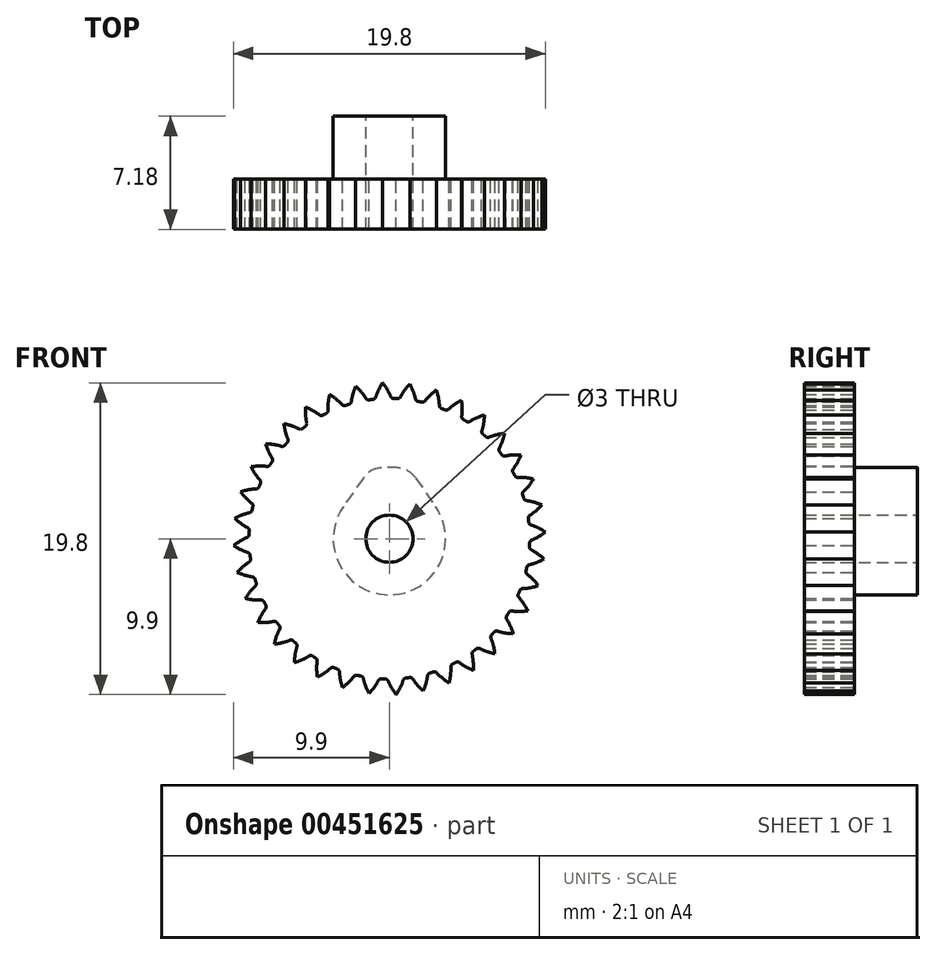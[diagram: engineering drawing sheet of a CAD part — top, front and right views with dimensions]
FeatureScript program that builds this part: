
annotation { "Feature Type Name" : "Feature", "Feature Type Description" : "" }
export const myFeature = defineFeature(function(context is Context, id is Id, definition is map)
    precondition{}
    {
        {
            assignVariable(context, id + "F0", {"name" : "Teeth", "anyValue" : 36});
        }
        {
            var Q0;
            Q0=qCreatedBy(makeId("Front.planeOp"),FACE);
            var sketch = newSketch(context, id + "F1", { "sketchPlane" : qUnion([Q0])});
            skCircle(sketch, "E0", {"center": v(0, 0) * mm, "radius": 8.49 * mm, "construction": true});
            skLineSegment(sketch, "E1", {"start": v(0, 0) * mm, "end": v(-0.32, 8.48) * mm, "construction": true});
            skLineSegment(sketch, "E2", {"start": v(0, 0) * mm, "end": v(-0.87, 8.44) * mm, "construction": true});
            skLineSegment(sketch, "E3", {"start": v(0, 0) * mm, "end": v(-1.41, 8.37) * mm, "construction": true});
            skLineSegment(sketch, "E4", {"start": v(-1.41, 8.37) * mm, "end": v(0.2, 8.64) * mm, "construction": true});
            skLineSegment(sketch, "E5", {"start": v(0, 0) * mm, "end": v(-1.95, 8.26) * mm, "construction": true});
            skLineSegment(sketch, "E6", {"start": v(-1.95, 8.26) * mm, "end": v(0.18, 8.76) * mm, "construction": true});
            skLineSegment(sketch, "E7", {"start": v(-1.41, 8.37) * mm, "end": v(-0.87, 8.44) * mm, "construction": true});
            skLineSegment(sketch, "E8", {"start": v(-1.95, 8.26) * mm, "end": v(-1.41, 8.37) * mm, "construction": true});
            skLineSegment(sketch, "E9", {"start": v(-1.41, 8.37) * mm, "end": v(-0.32, 8.48) * mm, "construction": true});
            skLineSegment(sketch, "E10", {"start": v(-1.95, 8.26) * mm, "end": v(-0.32, 8.48) * mm, "construction": true});
            skLineSegment(sketch, "E11", {"start": v(0, 0) * mm, "end": v(-3.5, 7.73) * mm, "construction": true});
            skLineSegment(sketch, "E12", {"start": v(-3.5, 7.73) * mm, "end": v(-0.04, 9.3) * mm, "construction": true});
            skLineSegment(sketch, "E13", {"start": v(0, 0) * mm, "end": v(-3, 7.94) * mm, "construction": true});
            skLineSegment(sketch, "E14", {"start": v(-3, 7.94) * mm, "end": v(0.06, 9.1) * mm, "construction": true});
            skLineSegment(sketch, "E15", {"start": v(0, 0) * mm, "end": v(-2.48, 8.12) * mm, "construction": true});
            skLineSegment(sketch, "E16", {"start": v(-2.48, 8.12) * mm, "end": v(0.13, 8.91) * mm, "construction": true});
            skLineSegment(sketch, "E17", {"start": v(-2.48, 8.12) * mm, "end": v(-1.95, 8.26) * mm, "construction": true});
            skLineSegment(sketch, "E18", {"start": v(-2.48, 8.12) * mm, "end": v(-3, 7.94) * mm, "construction": true});
            skLineSegment(sketch, "E19", {"start": v(-3, 7.94) * mm, "end": v(-3.5, 7.73) * mm, "construction": true});
            skLineSegment(sketch, "E20", {"start": v(-2.48, 8.12) * mm, "end": v(-0.32, 8.48) * mm, "construction": true});
            skLineSegment(sketch, "E21", {"start": v(-3, 7.94) * mm, "end": v(-0.32, 8.48) * mm, "construction": true});
            skLineSegment(sketch, "E22", {"start": v(-3.5, 7.73) * mm, "end": v(-0.32, 8.48) * mm, "construction": true});
            skLineSegment(sketch, "E23", {"start": v(0, 0) * mm, "end": v(-4.47, 7.21) * mm, "construction": true});
            skLineSegment(sketch, "E24", {"start": v(-4.47, 7.21) * mm, "end": v(-0.34, 9.78) * mm, "construction": true});
            skLineSegment(sketch, "E25", {"start": v(0, 0) * mm, "end": v(-4.93, 6.9) * mm, "construction": true});
            skLineSegment(sketch, "E26", {"start": v(-4.93, 6.9) * mm, "end": v(-0.54, 10.04) * mm, "construction": true});
            skLineSegment(sketch, "E27", {"start": v(0, 0) * mm, "end": v(-5.37, 6.58) * mm, "construction": true});
            skLineSegment(sketch, "E28", {"start": v(0, 0) * mm, "end": v(-4, 7.49) * mm, "construction": true});
            skLineSegment(sketch, "E29", {"start": v(-4, 7.49) * mm, "end": v(-0.17, 9.53) * mm, "construction": true});
            skLineSegment(sketch, "E30", {"start": v(-3.5, 7.73) * mm, "end": v(-4, 7.49) * mm, "construction": true});
            skLineSegment(sketch, "E31", {"start": v(-4, 7.49) * mm, "end": v(-4.47, 7.21) * mm, "construction": true});
            skLineSegment(sketch, "E32", {"start": v(-4.47, 7.21) * mm, "end": v(-4.93, 6.9) * mm, "construction": true});
            skLineSegment(sketch, "E33", {"start": v(-4.93, 6.9) * mm, "end": v(-5.37, 6.58) * mm, "construction": true});
            skLineSegment(sketch, "E34", {"start": v(-0.32, 8.48) * mm, "end": v(-4, 7.49) * mm, "construction": true});
            skLineSegment(sketch, "E35", {"start": v(-0.32, 8.48) * mm, "end": v(-4.47, 7.21) * mm, "construction": true});
            skLineSegment(sketch, "E36", {"start": v(-0.32, 8.48) * mm, "end": v(-4.93, 6.9) * mm, "construction": true});
            skLineSegment(sketch, "E37", {"start": v(-0.32, 8.48) * mm, "end": v(-5.37, 6.58) * mm, "construction": true});
            skCircle(sketch, "E38", {"center": v(0, 0) * mm, "radius": 9.53 * mm, "construction": true});
            skCircle(sketch, "E39", {"center": v(0, 0) * mm, "radius": 10.05 * mm});
            skPoint(sketch, "E40", {"position": v(0, 9.53) * mm});
            skLineSegment(sketch, "E41", {"start": v(0, 0) * mm, "end": v(-0.38, 8.6) * mm, "construction": true});
            skPoint(sketch, "E42.MirrorP", {"position": v(-0.83, 9.49) * mm});
            skLineSegment(sketch, "E43", {"start": v(-0.83, 9.49) * mm, "end": v(0, 0) * mm, "construction": true});
            skLineSegment(sketch, "E44", {"start": v(0, 0) * mm, "end": v(0, 9.53) * mm, "construction": true});
            skLineSegment(sketch, "E45", {"start": v(-0.87, 8.44) * mm, "end": v(-0.32, 8.48) * mm, "construction": true});
            skLineSegment(sketch, "E46", {"start": v(0.2, 8.64) * mm, "end": v(0.18, 8.76) * mm, "construction": true});
            skLineSegment(sketch, "E47", {"start": v(0, 0) * mm, "end": v(0, 10.19) * mm, "construction": true});
            skCircle(sketch, "E48", {"center": v(0, 0) * mm, "radius": 8.91 * mm});
            skSolve(sketch);
        }
        {
            var Q0;
            Q0=qCreatedBy(makeId("Front.planeOp"),FACE);
            var sketch = newSketch(context, id + "F2", { "sketchPlane" : qUnion([Q0])});
            skCircle(sketch, "E49.0", {"center": v(0, 0) * mm, "radius": 9.53 * mm, "construction": true});
            skPoint(sketch, "E50.0", {"position": v(-0.54, 10.04) * mm});
            skPoint(sketch, "E50.1", {"position": v(-0.34, 9.78) * mm});
            skPoint(sketch, "E50.2", {"position": v(-0.17, 9.53) * mm});
            skPoint(sketch, "E50.3", {"position": v(-0.04, 9.3) * mm});
            skPoint(sketch, "E50.4", {"position": v(0.06, 9.1) * mm});
            skPoint(sketch, "E50.6", {"position": v(0.18, 8.76) * mm});
            skPoint(sketch, "E50.7", {"position": v(0.2, 8.64) * mm});
            skPoint(sketch, "E50.8", {"position": v(0.13, 8.91) * mm});
            skLineSegment(sketch, "E51.0", {"start": v(0, 0) * mm, "end": v(-0.38, 8.6) * mm, "construction": true});
            skFitSpline(sketch, "E52", {"points": [v(-0.54, 10.04) * mm, v(-0.34, 9.78) * mm, v(-0.17, 9.53) * mm, v(-0.04, 9.3) * mm, v(0.06, 9.1) * mm, v(0.13, 8.91) * mm, v(0.18, 8.76) * mm, v(0.2, 8.64) * mm], "startDerivative": vector(3.53, -4.5) * mm, "endDerivative": vector(0.8, -3.4) * mm});
            skFitSpline(sketch, "E53.MirrorCS", {"points": [v(-0.34, 10.05) * mm, v(-0.52, 9.77) * mm, v(-0.66, 9.5) * mm, v(-0.77, 9.27) * mm, v(-0.85, 9.06) * mm, v(-0.9, 8.87) * mm, v(-0.94, 8.71) * mm, v(-0.96, 8.6) * mm], "startDerivative": vector(-3.13, -4.8) * mm, "endDerivative": vector(-0.5, -3.46) * mm});
            skCircle(sketch, "E54", {"center": v(0, 0) * mm, "radius": 1.5 * mm});
            skCircle(sketch, "E55.0", {"center": v(0, 0) * mm, "radius": 8.91 * mm});
            skArc(sketch, "E56", {"start": v(-0.54, 10.04) * mm, "mid": v(0.44, -10.04) * mm, "end": v(-0.34, 10.05) * mm});
            skLineSegment(sketch, "E57", {"start": v(-0.96, 8.6) * mm, "end": v(0, 0) * mm});
            skLineSegment(sketch, "E58", {"start": v(0, 0) * mm, "end": v(0.2, 8.64) * mm});
            skSolve(sketch);
        }
        {
            var Q0;
            {var subQ1=sQuery(id+"F2.wireOp",EDGE,"E52");var subQ9=sQuery(id+"F2.wireOp",EDGE,"rA0usyOi-Jm6w-jZNR-JSDv-ujEcH4bsm2Ol");var subQ11=makeQuery(id+"F2.imprint","INTERSECT",VERTEX,{"derivedFrom":[subQ1,subQ9]});Q0=makeQuery(id+"F2.imprint","IMPRINT",FACE,{"disambiguationData":[TD([[makeQuery(id+"F2.imprint","IMPRINT",EDGE,{"disambiguationData":[TD([[subQ11,1.0]])],"derivedFrom":subQ1}),-1.0]])]});}
            var Q1;
            {var subQ0=sQuery(id+"F2.wireOp",EDGE,"QqPcIgQ4-TZE6-73E5-WQaq-ugCT5JtziKyn");var subQ1=sQuery(id+"F2.wireOp",EDGE,"90be38e0-c88f-493d-85a8-1201295b9109.0");var subQ2=makeQuery(id+"F2.imprint","INTERSECT",VERTEX,{"derivedFrom":[subQ1,subQ0]});Q1=makeQuery(id+"F2.imprint","IMPRINT",FACE,{"disambiguationData":[TD([[makeQuery(id+"F2.imprint","IMPRINT",EDGE,{"disambiguationData":[TD([[subQ2,1.0]])],"derivedFrom":subQ1}),1.0]])]});}
            var Q2;
            {var subQ0=sQuery(id+"F2.wireOp",EDGE,"QqPcIgQ4-TZE6-73E5-WQaq-ugCT5JtziKyn");var subQ1=sQuery(id+"F2.wireOp",EDGE,"90be38e0-c88f-493d-85a8-1201295b9109.0");var subQ2=makeQuery(id+"F2.imprint","INTERSECT",VERTEX,{"derivedFrom":[subQ1,subQ0]});Q2=makeQuery(id+"F2.imprint","IMPRINT",FACE,{"disambiguationData":[TD([[makeQuery(id+"F2.imprint","IMPRINT",EDGE,{"disambiguationData":[TD([[subQ2,-1.0]])],"derivedFrom":subQ1}),1.0]])]});}
            var Q3;
            {var subQ1=sQuery(id+"F2.wireOp",EDGE,"E52");var subQ8=sQuery(id+"F2.wireOp",EDGE,"b861a5ab-cd51-40f1-92ab-cea0f5fe0d4d.1");var subQ11=makeQuery(id+"F2.imprint","INTERSECT",VERTEX,{"derivedFrom":[subQ1,subQ8]});Q3=makeQuery(id+"F2.imprint","IMPRINT",FACE,{"disambiguationData":[TD([[makeQuery(id+"F2.imprint","IMPRINT",EDGE,{"disambiguationData":[TD([[subQ11,1.0]])],"derivedFrom":subQ1}),-1.0]])]});}
            var Q4;
            {var subQ0=sQuery(id+"F2.wireOp",EDGE,"b861a5ab-cd51-40f1-92ab-cea0f5fe0d4d.0");var subQ1=sQuery(id+"F2.wireOp",EDGE,"E54");var subQ2=makeQuery(id+"F2.imprint","INTERSECT",VERTEX,{"derivedFrom":[subQ1,subQ0]});Q4=makeQuery(id+"F2.imprint","IMPRINT",FACE,{"disambiguationData":[TD([[makeQuery(id+"F2.imprint","IMPRINT",EDGE,{"disambiguationData":[TD([[subQ2,-1.0]])],"derivedFrom":subQ1}),-1.0]])]});}
            var Q5;
            {var subQ0=sQuery(id+"F2.wireOp",EDGE,"b861a5ab-cd51-40f1-92ab-cea0f5fe0d4d.0");var subQ1=sQuery(id+"F2.wireOp",EDGE,"E54");var subQ2=makeQuery(id+"F2.imprint","INTERSECT",VERTEX,{"derivedFrom":[subQ1,subQ0]});Q5=makeQuery(id+"F2.imprint","IMPRINT",FACE,{"disambiguationData":[TD([[makeQuery(id+"F2.imprint","IMPRINT",EDGE,{"disambiguationData":[TD([[subQ2,1.0]])],"derivedFrom":subQ1}),-1.0]])]});}
            extrude(context, id + "F3", {"entities" : qUnion([Q0, Q1, Q2, Q3, Q4, Q5]), "depth" : 3.17 * mm});
        }
        {
            var Q0;
            Q0=makeQuery(id+"F3.opExtrude","SWEPT_EDGE",EDGE,{"disambiguationData":[OSD([sQuery(id+"F2.wireOp",EDGE,"b861a5ab-cd51-40f1-92ab-cea0f5fe0d4d.1"),sQuery(id+"F2.wireOp",EDGE,"E55.0")])]});
            var Q1;
            Q1=makeQuery(id+"F3.opExtrude","SWEPT_EDGE",EDGE,{"disambiguationData":[OSD([sQuery(id+"F2.wireOp",EDGE,"b861a5ab-cd51-40f1-92ab-cea0f5fe0d4d.0"),sQuery(id+"F2.wireOp",EDGE,"E55.0")])]});
            fillet(context, id + "F4", {"entities" : qUnion([Q0, Q1]), "radius" : 0.2 * mm, "tangentPropagation" : true, "allowEdgeOverflow" : false});
        }
        {
            var Q0;
            Q0=makeQuery(id+"F4.opFillet","BLEND_FACE",FACE,{"disambiguationData":[OSD([sQuery(id+"F2.wireOp",EDGE,"E55.0"),sQuery(id+"F2.wireOp",EDGE,"E57")])]});
            var Q1;
            Q1=makeQuery(id+"F3.opExtrude","SWEPT_FACE",FACE,{"disambiguationData":[OSD([sQuery(id+"F2.wireOp",EDGE,"E57")])]});
            var Q2;
            Q2=makeQuery(id+"F3.opExtrude","SWEPT_FACE",FACE,{"disambiguationData":[OSD([sQuery(id+"F2.wireOp",EDGE,"E53.MirrorCS")])]});
            var Q3;
            Q3=makeQuery(id+"F3.opExtrude","SWEPT_FACE",FACE,{"disambiguationData":[OSD([sQuery(id+"F2.wireOp",EDGE,"E56")])]});
            var Q4;
            Q4=makeQuery(id+"F3.opExtrude","SWEPT_FACE",FACE,{"disambiguationData":[OSD([sQuery(id+"F2.wireOp",EDGE,"E52")])]});
            var Q5;
            Q5=makeQuery(id+"F3.opExtrude","SWEPT_FACE",FACE,{"disambiguationData":[OSD([sQuery(id+"F2.wireOp",EDGE,"E58")])]});
            var Q6;
            Q6=makeQuery(id+"F4.opFillet","BLEND_FACE",FACE,{"disambiguationData":[OSD([sQuery(id+"F2.wireOp",EDGE,"E55.0"),sQuery(id+"F2.wireOp",EDGE,"E58")])]});
            var Q7;
            Q7=makeQuery(id+"F3.opExtrude","SWEPT_FACE",FACE,{"disambiguationData":[OSD([sQuery(id+"F2.wireOp",EDGE,"E55.0")])]});
            circularPattern(context, id + "F5", {"faces" : qUnion([Q0, Q1, Q2, Q3, Q4, Q5, Q6]), "axis" : qUnion([Q7]), "angle" : 360 * degree, "instanceCount" : round(getVariable(context, 'Teeth')), "equalSpace" : true, "patternType" : PatternType.FACE});
        }
        {
            var Q0;
            Q0=makeQuery(id+"F3.opExtrude","CAP_FACE",FACE,{"disambiguationData":[OSD([sQuery(id+"F2.wireOp",EDGE,"E52"),sQuery(id+"F2.wireOp",EDGE,"E53.MirrorCS"),sQuery(id+"F2.wireOp",EDGE,"E54"),sQuery(id+"F2.wireOp",EDGE,"E55.0")])],"isStart":true});
            var sketch = newSketch(context, id + "F6", { "sketchPlane" : qUnion([Q0])});
            skCircle(sketch, "E59", {"center": v(0, 0) * mm, "radius": 3.57 * mm});
            skArc(sketch, "E60", {"start": v(1.33, 4.34) * mm, "mid": v(0, 4.54) * mm, "end": v(-1.33, 4.34) * mm});
            skLineSegment(sketch, "E61", {"start": v(0, 0) * mm, "end": v(0, 6.8) * mm, "construction": true});
            skLineSegment(sketch, "E62", {"start": v(0, 4.54) * mm, "end": v(-1.33, 4.54) * mm, "construction": true});
            skLineSegment(sketch, "E63", {"start": v(0, 4.54) * mm, "end": v(1.33, 4.54) * mm, "construction": true});
            skLineSegment(sketch, "E64", {"start": v(-1.33, 4.54) * mm, "end": v(-1.33, 0) * mm, "construction": true});
            skLineSegment(sketch, "E65", {"start": v(1.33, 4.54) * mm, "end": v(1.33, 0) * mm, "construction": true});
            skPoint(sketch, "E66", {"position": v(-1.33, 4.34) * mm});
            skPoint(sketch, "E67", {"position": v(1.33, 4.34) * mm});
            skLineSegment(sketch, "E68", {"start": v(-1.33, 4.34) * mm, "end": v(-2.93, 2.04) * mm});
            skLineSegment(sketch, "E69", {"start": v(1.33, 4.34) * mm, "end": v(2.93, 2.04) * mm});
            skSolve(sketch);
        }
        {
            var Q0;
            Q0=makeQuery(id+"F6.imprint","IMPRINT",FACE,{"disambiguationData":[TD([[makeQuery(id+"F6.imprint","IMPRINT",EDGE,{"derivedFrom":makeQuery(id+"F3.opExtrude","CAP_EDGE",EDGE,{"disambiguationData":[OSD([sQuery(id+"F2.wireOp",EDGE,"E54")])],"isStart":true})}),1.0]])]});
            var Q1;
            Q1=makeQuery(id+"F6.imprint","IMPRINT",FACE,{"disambiguationData":[TD([[makeQuery(id+"F6.imprint","IMPRINT",EDGE,{"derivedFrom":sQuery(id+"F6.wireOp",EDGE,"E60")}),1.0]])]});
            extrude(context, id + "F7", {"entities" : qUnion([Q0, Q1]), "operationType" : NewBodyOperationType.ADD, "depth" : 4 * mm});
        }
        {
            var Q0;
            Q0=makeQuery(id+"F6.imprint","IMPRINT",FACE,{"disambiguationData":[TD([[makeQuery(id+"F6.imprint","IMPRINT",EDGE,{"derivedFrom":makeQuery(id+"F3.opExtrude","CAP_EDGE",EDGE,{"disambiguationData":[OSD([sQuery(id+"F2.wireOp",EDGE,"E54")])],"isStart":true})}),-1.0]])]});
            extrude(context, id + "F8", {"entities" : qUnion([Q0]), "operationType" : NewBodyOperationType.REMOVE, "endBound" : BoundingType.SYMMETRIC, "depth" : 25 * mm});
        }
        {
            var Q0;
            Q0=makeQuery(id+"F7.opExtrude","SWEPT_EDGE",EDGE,{"disambiguationData":[OSD([sQuery(id+"F6.wireOp",EDGE,"E60"),sQuery(id+"F6.wireOp",EDGE,"E69")])]});
            var Q1;
            Q1=makeQuery(id+"F7.opExtrude","SWEPT_EDGE",EDGE,{"disambiguationData":[OSD([sQuery(id+"F6.wireOp",EDGE,"E60"),sQuery(id+"F6.wireOp",EDGE,"E68")])]});
            fillet(context, id + "F9", {"entities" : qUnion([Q0, Q1]), "radius" : 1.5 * mm, "tangentPropagation" : true, "allowEdgeOverflow" : false});
        }
    });
